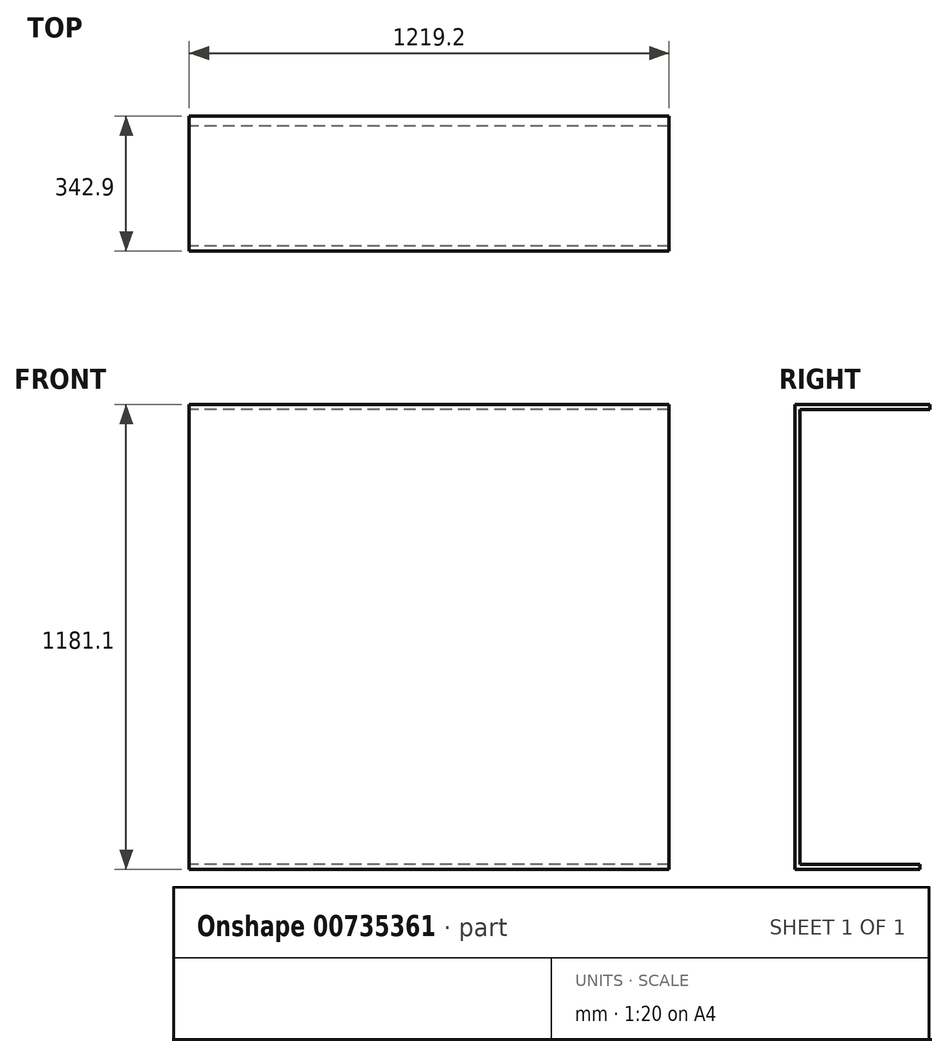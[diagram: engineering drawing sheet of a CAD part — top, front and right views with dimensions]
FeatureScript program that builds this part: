
annotation { "Feature Type Name" : "Feature", "Feature Type Description" : "" }
export const myFeature = defineFeature(function(context is Context, id is Id, definition is map)
    precondition{}
    {
        {
            var Q0;
            Q0=qCreatedBy(makeId("Right.planeOp"),FACE);
            var sketch = newSketch(context, id + "F0", { "sketchPlane" : qUnion([Q0])});
            skLineSegment(sketch, "E0", {"start": v(-1206.28, 842.47) * mm, "end": v(-863.38, 842.47) * mm});
            skLineSegment(sketch, "E1", {"start": v(-863.38, 842.47) * mm, "end": v(-863.38, 829.77) * mm});
            skLineSegment(sketch, "E2", {"start": v(-863.38, 829.77) * mm, "end": v(-1193.58, 829.77) * mm});
            skLineSegment(sketch, "E3", {"start": v(-1193.58, 829.77) * mm, "end": v(-1193.58, -325.93) * mm});
            skLineSegment(sketch, "E4", {"start": v(-1193.58, -325.93) * mm, "end": v(-888.78, -325.93) * mm});
            skLineSegment(sketch, "E5", {"start": v(-888.78, -325.93) * mm, "end": v(-888.78, -338.63) * mm});
            skLineSegment(sketch, "E6", {"start": v(-888.78, -338.63) * mm, "end": v(-1206.28, -338.63) * mm});
            skLineSegment(sketch, "E7", {"start": v(-1206.28, -338.63) * mm, "end": v(-1206.28, 842.47) * mm});
            skSolve(sketch);
        }
        {
            var Q0;
            Q0 = qSketchRegion(id + "F0", true);
            extrude(context, id + "F1", {"entities" : qUnion([Q0]), "depth" : 1219.2 * mm, "offsetDistance" : 25.4 * mm});
        }
    });
